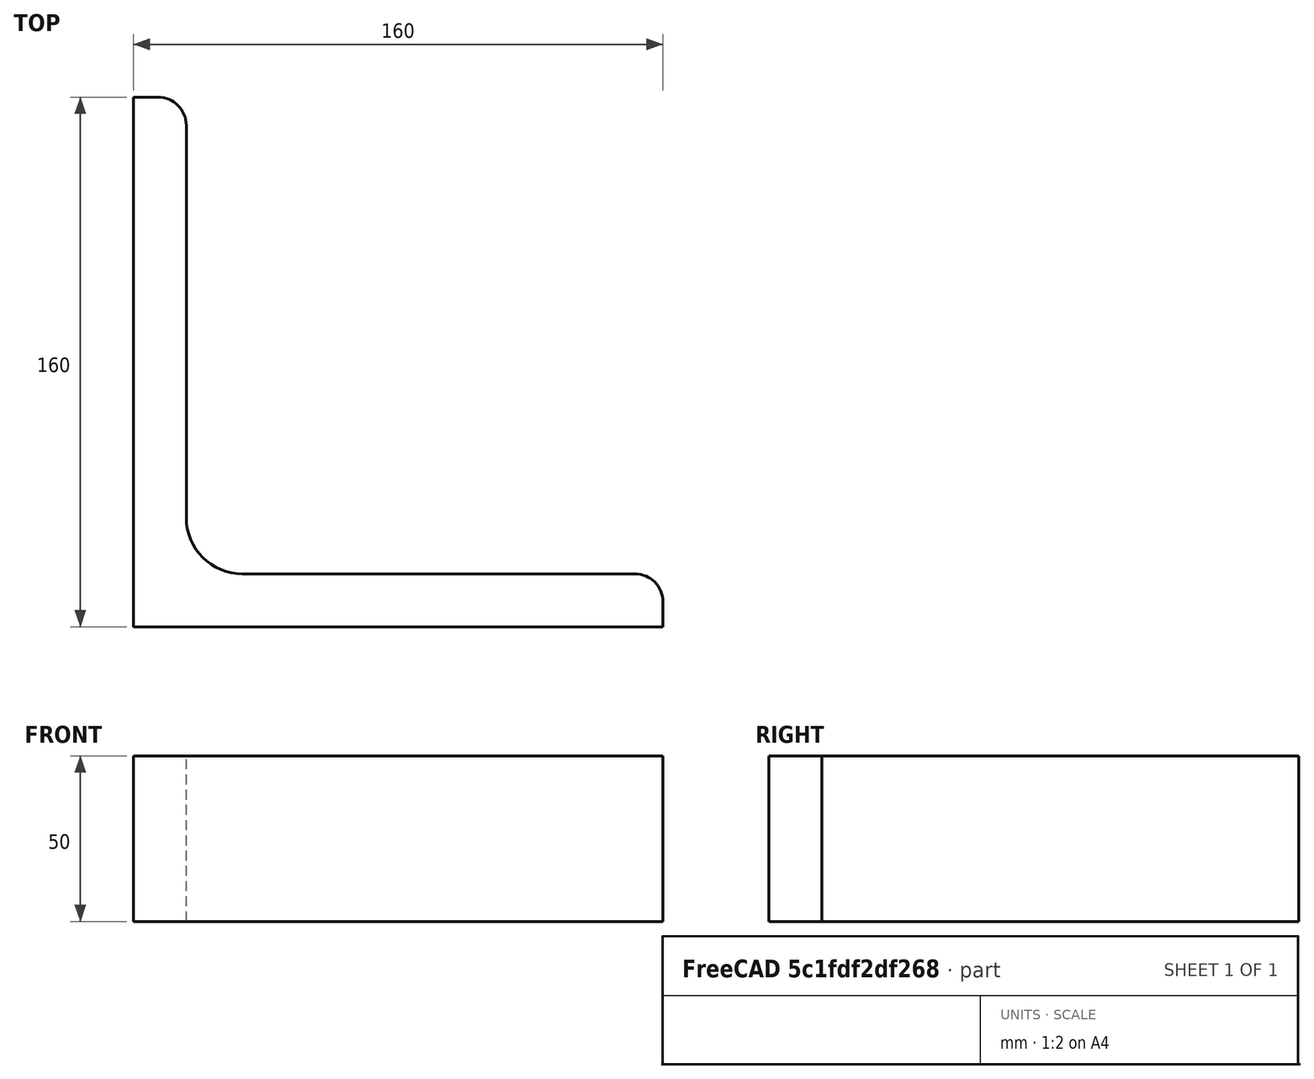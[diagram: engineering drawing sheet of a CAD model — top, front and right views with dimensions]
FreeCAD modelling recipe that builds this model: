
FCSTD DOCUMENT  (FreeCAD 0.15R4671 (Git))
Label: Angle Bar L160x160x16 EN10056 S235JR
License: All rights reserved
LicenseURL: http://en.wikipedia.org/wiki/All_rights_reserved
objects: Sketcher::SketchObject×1, Part::Extrusion×1
note: 2 computed .brp shape members not serialized (recipe doc carries the construction recipe); baked Part::Feature solids carry a one-line shape summary decoded from their .brp

FEATURE [Sketcher::SketchObject] Sketch
  sketch-geometry (9):
    g0: LineSegment StartX=0 StartY=0 StartZ=0 EndX=160 EndY=0 EndZ=0
    g1: LineSegment StartX=160 StartY=0 StartZ=0 EndX=160 EndY=7.5 EndZ=0
    g2: LineSegment StartX=151.5 StartY=16 StartZ=0 EndX=33 EndY=16 EndZ=0
    g3: LineSegment StartX=0 StartY=0 StartZ=0 EndX=0 EndY=160 EndZ=0
    g4: LineSegment StartX=0 StartY=160 StartZ=0 EndX=7.5 EndY=160 EndZ=0
    g5: LineSegment StartX=16 StartY=151.5 StartZ=0 EndX=16 EndY=33 EndZ=0
    g6: ArcOfCircle CenterX=33 CenterY=33 CenterZ=0 NormalX=0 NormalY=0 NormalZ=1 Radius=17 StartAngle=3.14159 EndAngle=4.71239
    g7: ArcOfCircle CenterX=7.5 CenterY=151.5 CenterZ=0 NormalX=0 NormalY=0 NormalZ=1 Radius=8.5 StartAngle=0 EndAngle=1.5708
    g8: ArcOfCircle CenterX=151.5 CenterY=7.5 CenterZ=0 NormalX=0 NormalY=0 NormalZ=1 Radius=8.5 StartAngle=0 EndAngle=1.5708
  constraints (23):
    c: Coincident(g0,g-1)
    c: Horizontal(g0)
    c: Coincident(g1,g0)
    c: Vertical(g1)
    c: Horizontal(g2)
    c: Coincident(g3,g-1)
    c: Vertical(g3)
    c: Coincident(g4,g3)
    c: Horizontal(g4)
    c: Vertical(g5)
    c: Tangent(g5,g6) = -1.5708
    c: Tangent(g2,g6) = 1.5708
    c: Tangent(g4,g7) = 1.5708
    c: Tangent(g5,g7) = 1.5708
    c: Tangent(g2,g8) = -1.5708
    c: Tangent(g1,g8) = -1.5708
    c: DistanceX(g0) = 160
    c: DistanceY(g3) = 160
    c: DistanceY(g0,g2) = 16
    c: DistanceX(g3,g5) = 16
    c: Radius(g6) = 17
    c: Radius(g8) = 8.5
    c: Radius(g7) = 8.5
FEATURE [Part::Extrusion] Extrude  label="Angle Bar L160x160x16 EN10056 S235JR"
  Base = -> Sketch
  Dir = (0,0,50)
  Solid = true
